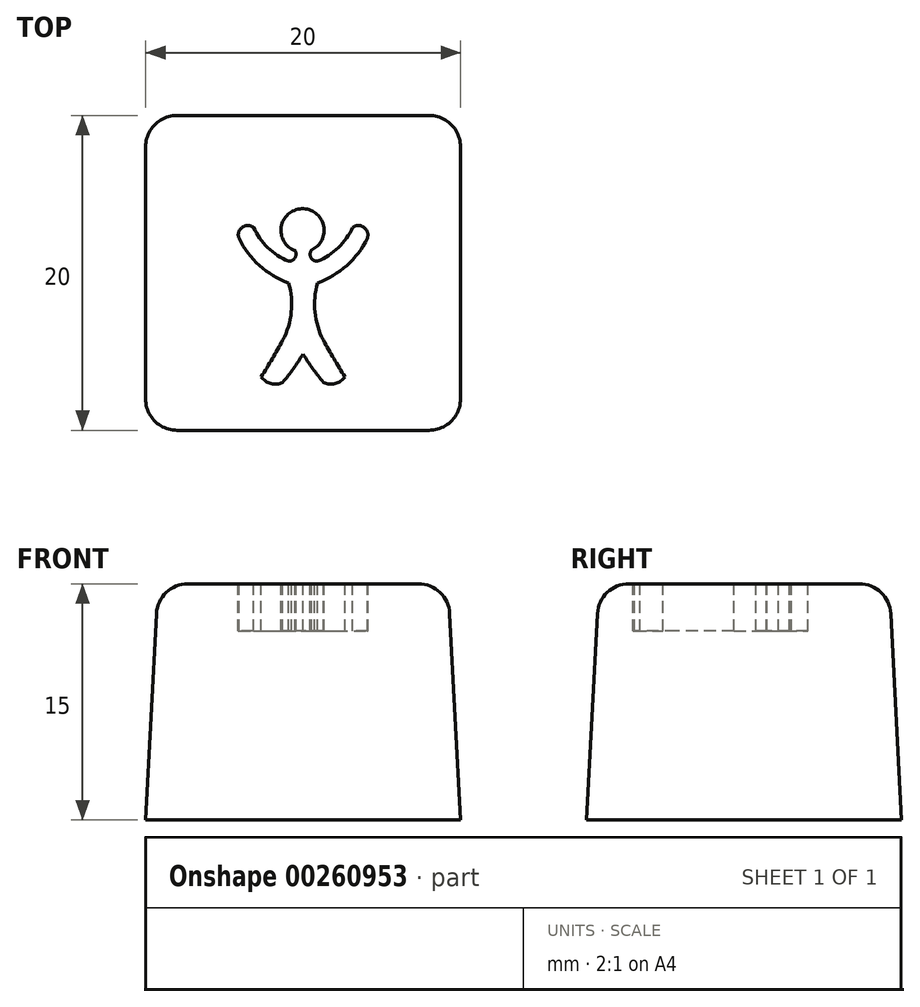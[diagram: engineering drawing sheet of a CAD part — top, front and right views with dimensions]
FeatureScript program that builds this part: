
annotation { "Feature Type Name" : "Feature", "Feature Type Description" : "" }
export const myFeature = defineFeature(function(context is Context, id is Id, definition is map)
    precondition{}
    {
        {
            var Q0;
            Q0=qCreatedBy(makeId("Top.planeOp"),FACE);
            var sketch = newSketch(context, id + "F0", { "sketchPlane" : qUnion([Q0])});
            skLineSegment(sketch, "E0.bottom", {"start": v(-9.42, 11.44) * mm, "end": v(10.58, 11.44) * mm});
            skLineSegment(sketch, "E0.top", {"start": v(-9.42, -8.56) * mm, "end": v(10.58, -8.56) * mm});
            skLineSegment(sketch, "E0.left", {"start": v(-9.42, 11.44) * mm, "end": v(-9.42, -8.56) * mm});
            skLineSegment(sketch, "E0.right", {"start": v(10.58, 11.44) * mm, "end": v(10.58, -8.56) * mm});
            skSolve(sketch);
        }
        {
            var Q0;
            Q0 = qSketchRegion(id + "F0", true);
            extrude(context, id + "F1", {"entities" : qUnion([Q0]), "depth" : 15 * mm, "hasDraft" : true, "draftAngle" : 3 * degree, "draftPullDirection" : true});
        }
        {
            var Q0;
            Q0=makeQuery(id+"F1.opExtrude","SWEPT_EDGE",EDGE,{"disambiguationData":[OSD([sQuery(id+"F0.wireOp",EDGE,"E0.bottom"),sQuery(id+"F0.wireOp",EDGE,"E0.right")])]});
            var Q1;
            Q1=makeQuery(id+"F1.opExtrude","SWEPT_EDGE",EDGE,{"disambiguationData":[OSD([sQuery(id+"F0.wireOp",EDGE,"E0.bottom"),sQuery(id+"F0.wireOp",EDGE,"E0.left")])]});
            var Q2;
            Q2=makeQuery(id+"F1.opExtrude","CAP_EDGE",EDGE,{"disambiguationData":[OSD([sQuery(id+"F0.wireOp",EDGE,"E0.bottom")])],"isStart":false});
            var Q3;
            Q3=makeQuery(id+"F1.opExtrude","CAP_EDGE",EDGE,{"disambiguationData":[OSD([sQuery(id+"F0.wireOp",EDGE,"E0.right")])],"isStart":false});
            var Q4;
            Q4=makeQuery(id+"F1.opExtrude","CAP_EDGE",EDGE,{"disambiguationData":[OSD([sQuery(id+"F0.wireOp",EDGE,"E0.left")])],"isStart":false});
            var Q5;
            Q5=makeQuery(id+"F1.opExtrude","CAP_EDGE",EDGE,{"disambiguationData":[OSD([sQuery(id+"F0.wireOp",EDGE,"E0.top")])],"isStart":false});
            var Q6;
            Q6=makeQuery(id+"F1.opExtrude","SWEPT_EDGE",EDGE,{"disambiguationData":[OSD([sQuery(id+"F0.wireOp",EDGE,"E0.top"),sQuery(id+"F0.wireOp",EDGE,"E0.right")])]});
            var Q7;
            Q7=makeQuery(id+"F1.opExtrude","SWEPT_EDGE",EDGE,{"disambiguationData":[OSD([sQuery(id+"F0.wireOp",EDGE,"E0.top"),sQuery(id+"F0.wireOp",EDGE,"E0.left")])]});
            fillet(context, id + "F2", {"entities" : qUnion([Q0, Q1, Q2, Q3, Q4, Q5, Q6, Q7]), "radius" : 2 * mm, "tangentPropagation" : true, "allowEdgeOverflow" : false});
        }
        {
            var Q0;
            Q0=makeQuery(id+"F1.opExtrude","CAP_FACE",FACE,{"disambiguationData":[OSD([sQuery(id+"F0.wireOp",EDGE,"E0.bottom"),sQuery(id+"F0.wireOp",EDGE,"E0.top"),sQuery(id+"F0.wireOp",EDGE,"E0.left"),sQuery(id+"F0.wireOp",EDGE,"E0.right")])],"isStart":false});
            var sketch = newSketch(context, id + "F3", { "sketchPlane" : qUnion([Q0])});
            skLineSegment(sketch, "E1", {"start": v(0.58, 7) * mm, "end": v(0.58, 6.76) * mm});
            skArc(sketch, "E2", {"start": v(-0.35, 2.18) * mm, "mid": v(0.06, 2.4) * mm, "end": v(0.07, 2.85) * mm});
            skArc(sketch, "E3", {"start": v(-2.57, 4.33) * mm, "mid": v(-1.67, 3.05) * mm, "end": v(-0.35, 2.18) * mm});
            skArc(sketch, "E4", {"start": v(-2.57, 4.33) * mm, "mid": v(-3.3, 4.34) * mm, "end": v(-3.5, 3.64) * mm});
            skArc(sketch, "E5", {"start": v(-3.5, 3.64) * mm, "mid": v(-2.2, 1.92) * mm, "end": v(-0.35, 0.8) * mm});
            skArc(sketch, "E6", {"start": v(-0.72, -2.83) * mm, "mid": v(-0.18, -1.05) * mm, "end": v(-0.35, 0.8) * mm});
            skArc(sketch, "E7", {"start": v(-2.09, -5.16) * mm, "mid": v(-1.38, -4) * mm, "end": v(-0.72, -2.83) * mm});
            skArc(sketch, "E8", {"start": v(-2.09, -5.16) * mm, "mid": v(-1.47, -5.59) * mm, "end": v(-0.72, -5.51) * mm});
            skArc(sketch, "E9", {"start": v(-0.72, -5.51) * mm, "mid": v(-0.04, -4.64) * mm, "end": v(0.58, -3.7) * mm});
            skArc(sketch, "E10.MirrorCS", {"start": v(1.5, 2.18) * mm, "mid": v(1.08, 2.41) * mm, "end": v(1.1, 2.89) * mm});
            skArc(sketch, "E11.MirrorCS", {"start": v(3.73, 4.33) * mm, "mid": v(2.82, 3.05) * mm, "end": v(1.5, 2.18) * mm});
            skArc(sketch, "E12.MirrorCS", {"start": v(3.73, 4.33) * mm, "mid": v(4.45, 4.34) * mm, "end": v(4.65, 3.64) * mm});
            skArc(sketch, "E13.MirrorCS", {"start": v(4.65, 3.64) * mm, "mid": v(3.35, 1.92) * mm, "end": v(1.5, 0.8) * mm});
            skArc(sketch, "E14.MirrorCS", {"start": v(1.87, -2.83) * mm, "mid": v(1.33, -1.05) * mm, "end": v(1.5, 0.8) * mm});
            skArc(sketch, "E15.MirrorCS", {"start": v(3.24, -5.16) * mm, "mid": v(2.53, -4) * mm, "end": v(1.87, -2.83) * mm});
            skArc(sketch, "E16.MirrorCS", {"start": v(3.24, -5.16) * mm, "mid": v(2.62, -5.59) * mm, "end": v(1.87, -5.51) * mm});
            skArc(sketch, "E17.MirrorCS", {"start": v(1.87, -5.51) * mm, "mid": v(1.19, -4.64) * mm, "end": v(0.58, -3.7) * mm});
            skPoint(sketch, "E18.MirrorCS.end.orphan", {"position": v(1.15, 2.95) * mm});
            skPoint(sketch, "E18.MirrorCS.start.orphan", {"position": v(0.58, 7) * mm});
            skPoint(sketch, "E19.orphan", {"position": v(0.58, 8.76) * mm});
            skPoint(sketch, "E20.trimOffspring.end.orphan", {"position": v(0.58, -5.87) * mm});
            skArc(sketch, "E21", {"start": v(1.1, 2.89) * mm, "mid": v(0.5, 5.51) * mm, "end": v(0.07, 2.85) * mm});
            skPoint(sketch, "E21.first.point", {"position": v(0.52, 2.77) * mm});
            skPoint(sketch, "E21.second.point", {"position": v(0.7, 5.5) * mm});
            skPoint(sketch, "E21.third.point", {"position": v(-0.24, 5.27) * mm});
            skPoint(sketch, "E22.orphan", {"position": v(0, 2.95) * mm});
            skSolve(sketch);
        }
        {
            var Q0;
            Q0=makeQuery(id+"F3.imprint","IMPRINT",FACE,{"disambiguationData":[TD([[makeQuery(id+"F3.imprint","IMPRINT",EDGE,{"derivedFrom":sQuery(id+"F3.wireOp",EDGE,"E2")}),-1.0]])]});
            extrude(context, id + "F4", {"entities" : qUnion([Q0]), "operationType" : NewBodyOperationType.REMOVE, "oppositeDirection" : true, "depth" : 3 * mm});
        }
    });
